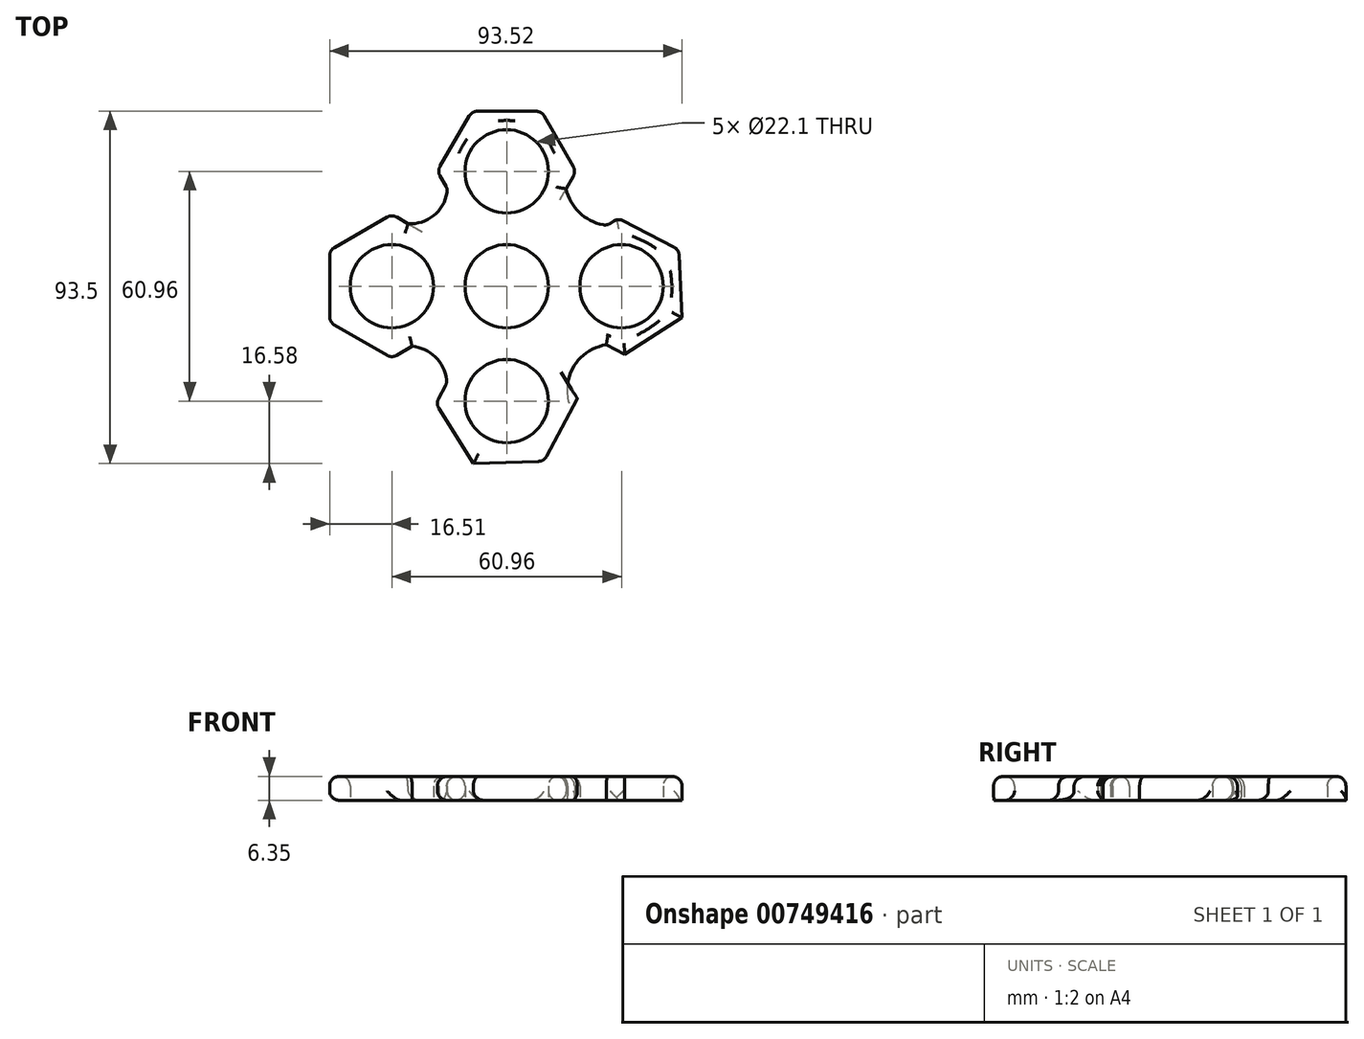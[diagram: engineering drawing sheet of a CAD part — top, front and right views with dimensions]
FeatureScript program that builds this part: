
annotation { "Feature Type Name" : "Feature", "Feature Type Description" : "" }
export const myFeature = defineFeature(function(context is Context, id is Id, definition is map)
    precondition{}
    {
        {
            var Q0;
            Q0=qCreatedBy(makeId("Top.planeOp"),FACE);
            var sketch = newSketch(context, id + "F0", { "sketchPlane" : qUnion([Q0])});
            skCircle(sketch, "E0", {"center": v(0, 0) * mm, "radius": 11.05 * mm});
            skCircle(sketch, "E1", {"center": v(0, 0) * mm, "radius": 13.97 * mm});
            skLineSegment(sketch, "E2", {"start": v(0, 0) * mm, "end": v(0, 30.48) * mm});
            skLineSegment(sketch, "E3", {"start": v(0, 0) * mm, "end": v(0, -30.48) * mm});
            skLineSegment(sketch, "E4", {"start": v(0, 0) * mm, "end": v(30.48, 0) * mm});
            skLineSegment(sketch, "E5", {"start": v(0, 0) * mm, "end": v(-30.48, 0) * mm});
            skCircle(sketch, "E6.cCircle", {"center": v(0, 30.48) * mm, "radius": 15.95 * mm, "construction": true});
            skLineSegment(sketch, "E6.0", {"start": v(18.42, 30.45) * mm, "end": v(9.18, 14.52) * mm});
            skLineSegment(sketch, "E6.1", {"start": v(9.18, 14.52) * mm, "end": v(-9.23, 14.54) * mm});
            skLineSegment(sketch, "E6.2", {"start": v(-9.23, 14.54) * mm, "end": v(-18.42, 30.5) * mm});
            skLineSegment(sketch, "E6.3", {"start": v(-18.42, 30.5) * mm, "end": v(-9.18, 46.44) * mm});
            skLineSegment(sketch, "E6.4", {"start": v(-9.18, 46.44) * mm, "end": v(9.23, 46.42) * mm});
            skLineSegment(sketch, "E6.5", {"start": v(9.23, 46.42) * mm, "end": v(18.42, 30.45) * mm});
            skPoint(sketch, "E6.0.midPoint", {"position": v(13.8, 22.48) * mm});
            skCircle(sketch, "E7.cCircle", {"center": v(30.48, 0) * mm, "radius": 15.65 * mm, "construction": true});
            skLineSegment(sketch, "E7.0", {"start": v(46.53, -8.3) * mm, "end": v(31.31, -18.05) * mm});
            skLineSegment(sketch, "E7.1", {"start": v(31.31, -18.05) * mm, "end": v(15.26, -9.75) * mm});
            skLineSegment(sketch, "E7.2", {"start": v(15.26, -9.75) * mm, "end": v(14.43, 8.3) * mm});
            skLineSegment(sketch, "E7.3", {"start": v(14.43, 8.3) * mm, "end": v(29.65, 18.05) * mm});
            skLineSegment(sketch, "E7.4", {"start": v(29.65, 18.05) * mm, "end": v(45.7, 9.75) * mm});
            skLineSegment(sketch, "E7.5", {"start": v(45.7, 9.75) * mm, "end": v(46.53, -8.3) * mm});
            skPoint(sketch, "E7.0.midPoint", {"position": v(38.92, -13.18) * mm});
            skCircle(sketch, "E8.cCircle", {"center": v(0, -30.48) * mm, "radius": 16.27 * mm, "construction": true});
            skLineSegment(sketch, "E8.0", {"start": v(8.83, -13.9) * mm, "end": v(18.78, -29.83) * mm});
            skLineSegment(sketch, "E8.1", {"start": v(18.78, -29.83) * mm, "end": v(9.95, -46.42) * mm});
            skLineSegment(sketch, "E8.2", {"start": v(9.95, -46.42) * mm, "end": v(-8.83, -47.06) * mm});
            skLineSegment(sketch, "E8.3", {"start": v(-8.83, -47.06) * mm, "end": v(-18.78, -31.13) * mm});
            skLineSegment(sketch, "E8.4", {"start": v(-18.78, -31.13) * mm, "end": v(-9.95, -14.54) * mm});
            skLineSegment(sketch, "E8.5", {"start": v(-9.95, -14.54) * mm, "end": v(8.83, -13.9) * mm});
            skPoint(sketch, "E8.0.midPoint", {"position": v(13.8, -21.86) * mm});
            skCircle(sketch, "E9.cCircle", {"center": v(-30.48, 0) * mm, "radius": 16.5 * mm, "construction": true});
            skLineSegment(sketch, "E9.0", {"start": v(-13.97, 9.53) * mm, "end": v(-13.97, -9.53) * mm});
            skLineSegment(sketch, "E9.1", {"start": v(-13.97, -9.53) * mm, "end": v(-30.48, -19.06) * mm});
            skLineSegment(sketch, "E9.2", {"start": v(-30.48, -19.06) * mm, "end": v(-46.99, -9.53) * mm});
            skLineSegment(sketch, "E9.3", {"start": v(-46.99, -9.53) * mm, "end": v(-47, 9.53) * mm});
            skLineSegment(sketch, "E9.4", {"start": v(-47, 9.53) * mm, "end": v(-30.48, 19.06) * mm});
            skLineSegment(sketch, "E9.5", {"start": v(-30.48, 19.06) * mm, "end": v(-13.97, 9.53) * mm});
            skPoint(sketch, "E9.0.midPoint", {"position": v(-13.97, 0) * mm});
            skCircle(sketch, "E10", {"center": v(0, 30.48) * mm, "radius": 11.05 * mm});
            skCircle(sketch, "E11", {"center": v(30.48, 0) * mm, "radius": 11.05 * mm});
            skCircle(sketch, "E12", {"center": v(0, -30.48) * mm, "radius": 11.05 * mm});
            skCircle(sketch, "E13", {"center": v(-30.48, 0) * mm, "radius": 11.05 * mm});
            skArc(sketch, "E14", {"start": v(15.56, 26.98) * mm, "mid": v(19.22, 19.62) * mm, "end": v(26.68, 16.15) * mm});
            skArc(sketch, "E15", {"start": v(26.44, -15.53) * mm, "mid": v(19.67, -18.96) * mm, "end": v(16.2, -25.71) * mm});
            skArc(sketch, "E16", {"start": v(-15.86, -25.65) * mm, "mid": v(-18.64, -19.04) * mm, "end": v(-25.1, -15.96) * mm});
            skArc(sketch, "E17", {"start": v(-26.18, 16.58) * mm, "mid": v(-19.03, 19.03) * mm, "end": v(-15.72, 25.82) * mm});
            skCircle(sketch, "E18", {"center": v(28.32, -27.66) * mm, "radius": 4.12 * mm});
            skCircle(sketch, "E19", {"center": v(27.89, 28.52) * mm, "radius": 4.13 * mm});
            skCircle(sketch, "E20", {"center": v(-25.93, -26) * mm, "radius": 4.13 * mm});
            skCircle(sketch, "E21", {"center": v(-25.56, 26.42) * mm, "radius": 4.13 * mm});
            skLineSegment(sketch, "E22", {"start": v(-30.48, -19.06) * mm, "end": v(-33.96, -33.34) * mm});
            skLineSegment(sketch, "E23", {"start": v(31.31, -18.05) * mm, "end": v(37.8, -34.28) * mm});
            skLineSegment(sketch, "E24", {"start": v(-33.96, -33.34) * mm, "end": v(-14.42, -38.1) * mm});
            skLineSegment(sketch, "E25", {"start": v(37.8, -34.28) * mm, "end": v(14.36, -38.12) * mm});
            skLineSegment(sketch, "E26", {"start": v(18.42, 30.45) * mm, "end": v(33.82, 39.31) * mm});
            skLineSegment(sketch, "E27", {"start": v(33.82, 39.31) * mm, "end": v(38.92, 13.18) * mm});
            skLineSegment(sketch, "E28", {"start": v(-30.48, 19.06) * mm, "end": v(-34.89, 34.58) * mm});
            skLineSegment(sketch, "E29", {"start": v(-34.89, 34.58) * mm, "end": v(-13.8, 38.48) * mm});
            skSolve(sketch);
        }
        {
            var Q0;
            {var subQ1=sQuery(id+"F0.wireOp",EDGE,"E6.4");Q0=makeQuery(id+"F0.imprint","IMPRINT",FACE,{"disambiguationData":[TD([[makeQuery(id+"F0.imprint","IMPRINT",EDGE,{"derivedFrom":subQ1}),-1.0]])]});}
            var Q1;
            {var subQ3=sQuery(id+"F0.wireOp",EDGE,"E1");var subQ10=sQuery(id+"F0.wireOp",EDGE,"E2");var subQ12=makeQuery(id+"F0.imprint","INTERSECT",VERTEX,{"derivedFrom":[subQ3,subQ10]});Q1=makeQuery(id+"F0.imprint","IMPRINT",FACE,{"disambiguationData":[TD([[makeQuery(id+"F0.imprint","IMPRINT",EDGE,{"disambiguationData":[TD([[subQ12,1.0]])],"derivedFrom":subQ3}),-1.0]])]});}
            var Q2;
            {var subQ0=sQuery(id+"F0.wireOp",EDGE,"E2");var subQ1=sQuery(id+"F0.wireOp",EDGE,"E0");var subQ2=makeQuery(id+"F0.imprint","INTERSECT",VERTEX,{"derivedFrom":[subQ1,subQ0]});Q2=makeQuery(id+"F0.imprint","IMPRINT",FACE,{"disambiguationData":[TD([[makeQuery(id+"F0.imprint","IMPRINT",EDGE,{"disambiguationData":[TD([[subQ2,1.0]])],"derivedFrom":subQ1}),-1.0]])]});}
            var Q3;
            {var subQ0=sQuery(id+"F0.wireOp",EDGE,"E9.2");Q3=makeQuery(id+"F0.imprint","IMPRINT",FACE,{"disambiguationData":[TD([[makeQuery(id+"F0.imprint","IMPRINT",EDGE,{"derivedFrom":subQ0}),-1.0]])]});}
            var Q4;
            {var subQ0=sQuery(id+"F0.wireOp",EDGE,"E2");var subQ1=sQuery(id+"F0.wireOp",EDGE,"E0");var subQ2=makeQuery(id+"F0.imprint","INTERSECT",VERTEX,{"derivedFrom":[subQ1,subQ0]});Q4=makeQuery(id+"F0.imprint","IMPRINT",FACE,{"disambiguationData":[TD([[makeQuery(id+"F0.imprint","IMPRINT",EDGE,{"disambiguationData":[TD([[subQ2,-1.0]])],"derivedFrom":subQ1}),-1.0]])]});}
            var Q5;
            {var subQ3=sQuery(id+"F0.wireOp",EDGE,"E17");Q5=makeQuery(id+"F0.imprint","IMPRINT",FACE,{"disambiguationData":[TD([[makeQuery(id+"F0.imprint","IMPRINT",EDGE,{"derivedFrom":subQ3}),-1.0]])]});}
            var Q6;
            {var subQ0=sQuery(id+"F0.wireOp",EDGE,"E5");var subQ1=sQuery(id+"F0.wireOp",EDGE,"E0");var subQ2=makeQuery(id+"F0.imprint","INTERSECT",VERTEX,{"derivedFrom":[subQ1,subQ0]});Q6=makeQuery(id+"F0.imprint","IMPRINT",FACE,{"disambiguationData":[TD([[makeQuery(id+"F0.imprint","IMPRINT",EDGE,{"disambiguationData":[TD([[subQ2,-1.0]])],"derivedFrom":subQ1}),-1.0]])]});}
            var Q7;
            {var subQ0=sQuery(id+"F0.wireOp",EDGE,"E4");var subQ1=sQuery(id+"F0.wireOp",EDGE,"E0");var subQ2=makeQuery(id+"F0.imprint","INTERSECT",VERTEX,{"derivedFrom":[subQ1,subQ0]});Q7=makeQuery(id+"F0.imprint","IMPRINT",FACE,{"disambiguationData":[TD([[makeQuery(id+"F0.imprint","IMPRINT",EDGE,{"disambiguationData":[TD([[subQ2,1.0]])],"derivedFrom":subQ1}),-1.0]])]});}
            var Q8;
            {var subQ3=sQuery(id+"F0.wireOp",EDGE,"E15");Q8=makeQuery(id+"F0.imprint","IMPRINT",FACE,{"disambiguationData":[TD([[makeQuery(id+"F0.imprint","IMPRINT",EDGE,{"derivedFrom":subQ3}),-1.0]])]});}
            var Q9;
            {var subQ8=sQuery(id+"F0.wireOp",EDGE,"E8.2");Q9=makeQuery(id+"F0.imprint","IMPRINT",FACE,{"disambiguationData":[TD([[makeQuery(id+"F0.imprint","IMPRINT",EDGE,{"derivedFrom":subQ8}),-1.0]])]});}
            var Q10;
            {var subQ3=sQuery(id+"F0.wireOp",EDGE,"E16");Q10=makeQuery(id+"F0.imprint","IMPRINT",FACE,{"disambiguationData":[TD([[makeQuery(id+"F0.imprint","IMPRINT",EDGE,{"derivedFrom":subQ3}),-1.0]])]});}
            var Q11;
            {var subQ9=sQuery(id+"F0.wireOp",EDGE,"E7.0");Q11=makeQuery(id+"F0.imprint","IMPRINT",FACE,{"disambiguationData":[TD([[makeQuery(id+"F0.imprint","IMPRINT",EDGE,{"derivedFrom":subQ9}),-1.0]])]});}
            extrude(context, id + "F1", {"entities" : qUnion([Q0, Q1, Q2, Q3, Q4, Q5, Q6, Q7, Q8, Q9, Q10, Q11]), "depth" : 6.35 * mm, "offsetDistance" : 25.4 * mm});
        }
        {
            var Q0;
            Q0=makeQuery(id+"F1.opExtrude","CAP_EDGE",EDGE,{"disambiguationData":[OSD([sQuery(id+"F0.wireOp",EDGE,"E9.4")])],"isStart":false});
            var Q1;
            Q1=makeQuery(id+"F1.opExtrude","CAP_EDGE",EDGE,{"disambiguationData":[OSD([sQuery(id+"F0.wireOp",EDGE,"E17")])],"isStart":false});
            var Q2;
            Q2=makeQuery(id+"F1.opExtrude","CAP_EDGE",EDGE,{"disambiguationData":[OSD([sQuery(id+"F0.wireOp",EDGE,"E9.5")])],"isStart":false});
            var Q3;
            Q3=makeQuery(id+"F1.opExtrude","CAP_EDGE",EDGE,{"disambiguationData":[OSD([sQuery(id+"F0.wireOp",EDGE,"E9.3")])],"isStart":false});
            var Q4;
            Q4=makeQuery(id+"F1.opExtrude","CAP_EDGE",EDGE,{"disambiguationData":[OSD([sQuery(id+"F0.wireOp",EDGE,"E8.2")])],"isStart":false});
            var Q5;
            Q5=makeQuery(id+"F1.opExtrude","CAP_EDGE",EDGE,{"disambiguationData":[OSD([sQuery(id+"F0.wireOp",EDGE,"E9.2")])],"isStart":false});
            var Q6;
            Q6=makeQuery(id+"F1.opExtrude","CAP_EDGE",EDGE,{"disambiguationData":[OSD([sQuery(id+"F0.wireOp",EDGE,"E8.1")])],"isStart":false});
            var Q7;
            Q7=makeQuery(id+"F1.opExtrude","CAP_EDGE",EDGE,{"disambiguationData":[OSD([sQuery(id+"F0.wireOp",EDGE,"E9.1")])],"isStart":false});
            var Q8;
            Q8=makeQuery(id+"F1.opExtrude","CAP_EDGE",EDGE,{"disambiguationData":[OSD([sQuery(id+"F0.wireOp",EDGE,"E16")])],"isStart":false});
            var Q9;
            Q9=makeQuery(id+"F1.opExtrude","CAP_EDGE",EDGE,{"disambiguationData":[OSD([sQuery(id+"F0.wireOp",EDGE,"E8.3")])],"isStart":false});
            var Q10;
            Q10=makeQuery(id+"F1.opExtrude","CAP_EDGE",EDGE,{"disambiguationData":[OSD([sQuery(id+"F0.wireOp",EDGE,"E8.4")])],"isStart":false});
            var Q11;
            Q11=makeQuery(id+"F1.opExtrude","CAP_EDGE",EDGE,{"disambiguationData":[OSD([sQuery(id+"F0.wireOp",EDGE,"E15")])],"isStart":false});
            var Q12;
            Q12=makeQuery(id+"F1.opExtrude","CAP_EDGE",EDGE,{"disambiguationData":[OSD([sQuery(id+"F0.wireOp",EDGE,"E6.3")])],"isStart":false});
            var Q13;
            Q13=makeQuery(id+"F1.opExtrude","CAP_EDGE",EDGE,{"disambiguationData":[OSD([sQuery(id+"F0.wireOp",EDGE,"E6.2")])],"isStart":false});
            var Q14;
            Q14=makeQuery(id+"F1.opExtrude","CAP_EDGE",EDGE,{"disambiguationData":[OSD([sQuery(id+"F0.wireOp",EDGE,"E6.4")])],"isStart":false});
            var Q15;
            Q15=makeQuery(id+"F1.opExtrude","CAP_EDGE",EDGE,{"disambiguationData":[OSD([sQuery(id+"F0.wireOp",EDGE,"E6.5")])],"isStart":false});
            var Q16;
            Q16=makeQuery(id+"F1.opExtrude","CAP_EDGE",EDGE,{"disambiguationData":[OSD([sQuery(id+"F0.wireOp",EDGE,"E6.0")])],"isStart":false});
            var Q17;
            Q17=makeQuery(id+"F1.opExtrude","CAP_EDGE",EDGE,{"disambiguationData":[OSD([sQuery(id+"F0.wireOp",EDGE,"E14")])],"isStart":false});
            var Q18;
            Q18=makeQuery(id+"F1.opExtrude","CAP_EDGE",EDGE,{"disambiguationData":[OSD([sQuery(id+"F0.wireOp",EDGE,"E7.3")])],"isStart":false});
            var Q19;
            Q19=makeQuery(id+"F1.opExtrude","CAP_EDGE",EDGE,{"disambiguationData":[OSD([sQuery(id+"F0.wireOp",EDGE,"E7.4")])],"isStart":false});
            var Q20;
            Q20=makeQuery(id+"F1.opExtrude","CAP_EDGE",EDGE,{"disambiguationData":[OSD([sQuery(id+"F0.wireOp",EDGE,"E7.5")])],"isStart":false});
            var Q21;
            Q21=makeQuery(id+"F1.opExtrude","CAP_EDGE",EDGE,{"disambiguationData":[OSD([sQuery(id+"F0.wireOp",EDGE,"E7.0")])],"isStart":false});
            var Q22;
            Q22=makeQuery(id+"F1.opExtrude","CAP_EDGE",EDGE,{"disambiguationData":[OSD([sQuery(id+"F0.wireOp",EDGE,"E7.1")])],"isStart":false});
            var Q23;
            Q23=makeQuery(id+"F1.opExtrude","CAP_EDGE",EDGE,{"disambiguationData":[OSD([sQuery(id+"F0.wireOp",EDGE,"E11")])],"isStart":false});
            var Q24;
            Q24=makeQuery(id+"F1.opExtrude","CAP_EDGE",EDGE,{"disambiguationData":[OSD([sQuery(id+"F0.wireOp",EDGE,"E10")])],"isStart":false});
            var Q25;
            Q25=makeQuery(id+"F1.opExtrude","CAP_EDGE",EDGE,{"disambiguationData":[OSD([sQuery(id+"F0.wireOp",EDGE,"E13")])],"isStart":false});
            var Q26;
            Q26=makeQuery(id+"F1.opExtrude","CAP_EDGE",EDGE,{"disambiguationData":[OSD([sQuery(id+"F0.wireOp",EDGE,"E0")])],"isStart":false});
            var Q27;
            Q27=makeQuery(id+"F1.opExtrude","CAP_EDGE",EDGE,{"disambiguationData":[OSD([sQuery(id+"F0.wireOp",EDGE,"E12")])],"isStart":false});
            var Q28;
            Q28=makeQuery(id+"F1.opExtrude","CAP_EDGE",EDGE,{"disambiguationData":[OSD([sQuery(id+"F0.wireOp",EDGE,"E12")])],"isStart":true});
            var Q29;
            Q29=makeQuery(id+"F1.opExtrude","CAP_EDGE",EDGE,{"disambiguationData":[OSD([sQuery(id+"F0.wireOp",EDGE,"E8.0")])],"isStart":true});
            var Q30;
            Q30=makeQuery(id+"F1.opExtrude","CAP_EDGE",EDGE,{"disambiguationData":[OSD([sQuery(id+"F0.wireOp",EDGE,"E8.4")])],"isStart":true});
            var Q31;
            Q31=makeQuery(id+"F1.opExtrude","CAP_EDGE",EDGE,{"disambiguationData":[OSD([sQuery(id+"F0.wireOp",EDGE,"E8.3")])],"isStart":true});
            var Q32;
            Q32=makeQuery(id+"F1.opExtrude","SWEPT_EDGE",EDGE,{"disambiguationData":[OSD([sQuery(id+"F0.wireOp",EDGE,"E8.4"),sQuery(id+"F0.wireOp",EDGE,"E16")])]});
            var Q33;
            Q33=makeQuery(id+"F1.opExtrude","SWEPT_EDGE",EDGE,{"disambiguationData":[OSD([sQuery(id+"F0.wireOp",EDGE,"E8.3"),sQuery(id+"F0.wireOp",EDGE,"E8.4")])]});
            var Q34;
            Q34=makeQuery(id+"F1.opExtrude","SWEPT_FACE",FACE,{"disambiguationData":[OSD([sQuery(id+"F0.wireOp",EDGE,"E9.2")])]});
            var Q35;
            Q35=makeQuery(id+"F1.opExtrude","SWEPT_EDGE",EDGE,{"disambiguationData":[OSD([sQuery(id+"F0.wireOp",EDGE,"E9.3"),sQuery(id+"F0.wireOp",EDGE,"E9.4")])]});
            var Q36;
            Q36=makeQuery(id+"F1.opExtrude","SWEPT_FACE",FACE,{"disambiguationData":[OSD([sQuery(id+"F0.wireOp",EDGE,"E9.4")])]});
            var Q37;
            Q37=makeQuery(id+"F1.opExtrude","SWEPT_EDGE",EDGE,{"disambiguationData":[OSD([sQuery(id+"F0.wireOp",EDGE,"E6.2"),sQuery(id+"F0.wireOp",EDGE,"E6.3")])]});
            var Q38;
            Q38=makeQuery(id+"F1.opExtrude","SWEPT_FACE",FACE,{"disambiguationData":[OSD([sQuery(id+"F0.wireOp",EDGE,"E6.3")])]});
            var Q39;
            Q39=makeQuery(id+"F1.opExtrude","CAP_EDGE",EDGE,{"disambiguationData":[OSD([sQuery(id+"F0.wireOp",EDGE,"E17")])],"isStart":true});
            var Q40;
            Q40=makeQuery(id+"F1.opExtrude","SWEPT_EDGE",EDGE,{"disambiguationData":[OSD([sQuery(id+"F0.wireOp",EDGE,"E6.2"),sQuery(id+"F0.wireOp",EDGE,"E17")])]});
            var Q41;
            Q41=makeQuery(id+"F1.opExtrude","CAP_EDGE",EDGE,{"disambiguationData":[OSD([sQuery(id+"F0.wireOp",EDGE,"E6.2")])],"isStart":true});
            var Q42;
            Q42=makeQuery(id+"F1.opExtrude","CAP_EDGE",EDGE,{"disambiguationData":[OSD([sQuery(id+"F0.wireOp",EDGE,"E9.3")])],"isStart":true});
            var Q43;
            Q43=makeQuery(id+"F1.opExtrude","SWEPT_FACE",FACE,{"disambiguationData":[OSD([sQuery(id+"F0.wireOp",EDGE,"E6.5")])]});
            var Q44;
            Q44=makeQuery(id+"F1.opExtrude","SWEPT_EDGE",EDGE,{"disambiguationData":[OSD([sQuery(id+"F0.wireOp",EDGE,"E7.3"),sQuery(id+"F0.wireOp",EDGE,"E14")])]});
            var Q45;
            Q45=makeQuery(id+"F1.opExtrude","SWEPT_EDGE",EDGE,{"disambiguationData":[OSD([sQuery(id+"F0.wireOp",EDGE,"E7.3"),sQuery(id+"F0.wireOp",EDGE,"E7.4")])]});
            var Q46;
            Q46=makeQuery(id+"F1.opExtrude","CAP_EDGE",EDGE,{"disambiguationData":[OSD([sQuery(id+"F0.wireOp",EDGE,"E7.4")])],"isStart":true});
            var Q47;
            Q47=makeQuery(id+"F1.opExtrude","CAP_EDGE",EDGE,{"disambiguationData":[OSD([sQuery(id+"F0.wireOp",EDGE,"E14")])],"isStart":true});
            var Q48;
            Q48=makeQuery(id+"F1.opExtrude","SWEPT_EDGE",EDGE,{"disambiguationData":[OSD([sQuery(id+"F0.wireOp",EDGE,"E7.4"),sQuery(id+"F0.wireOp",EDGE,"E7.5")])]});
            var Q49;
            Q49=makeQuery(id+"F1.opExtrude","SWEPT_EDGE",EDGE,{"disambiguationData":[OSD([sQuery(id+"F0.wireOp",EDGE,"E8.1"),sQuery(id+"F0.wireOp",EDGE,"E8.2")])]});
            fillet(context, id + "F2", {"entities" : qUnion([Q0, Q1, Q2, Q3, Q4, Q5, Q6, Q7, Q8, Q9, Q10, Q11, Q12, Q13, Q14, Q15, Q16, Q17, Q18, Q19, Q20, Q21, Q22, Q23, Q24, Q25, Q26, Q27, Q28, Q29, Q30, Q31, Q32, Q33, Q34, Q35, Q36, Q37, Q38, Q39, Q40, Q41, Q42, Q43, Q44, Q45, Q46, Q47, Q48, Q49]), "radius" : 2.54 * mm, "tangentPropagation" : true, "allowEdgeOverflow" : false});
        }
    });
